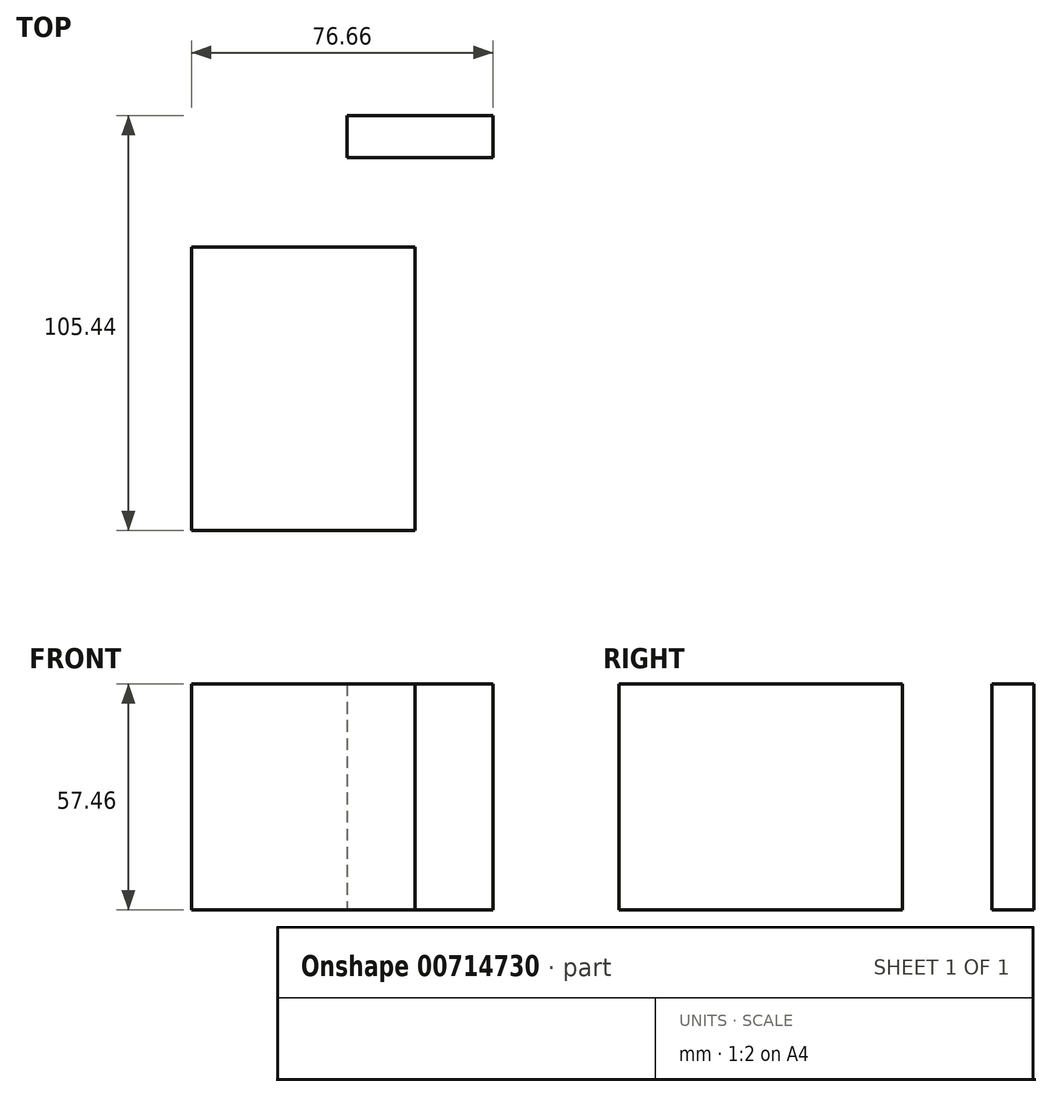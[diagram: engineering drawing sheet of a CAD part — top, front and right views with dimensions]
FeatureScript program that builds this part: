
annotation { "Feature Type Name" : "Feature", "Feature Type Description" : "" }
export const myFeature = defineFeature(function(context is Context, id is Id, definition is map)
    precondition{}
    {
        {
            var Q0;
            Q0=qCreatedBy(makeId("Top.planeOp"),FACE);
            var sketch = newSketch(context, id + "F0", { "sketchPlane" : qUnion([Q0])});
            skLineSegment(sketch, "E0.bottom", {"start": v(56.86, 0) * mm, "end": v(0, 0) * mm});
            skLineSegment(sketch, "E0.top", {"start": v(56.86, 72.05) * mm, "end": v(0, 72.05) * mm});
            skLineSegment(sketch, "E0.left", {"start": v(56.86, 0) * mm, "end": v(56.86, 72.05) * mm});
            skLineSegment(sketch, "E0.right", {"start": v(0, 0) * mm, "end": v(0, 72.05) * mm});
            skLineSegment(sketch, "E1.bottom", {"start": v(76.66, 94.67) * mm, "end": v(39.56, 94.67) * mm});
            skLineSegment(sketch, "E1.top", {"start": v(76.66, 105.44) * mm, "end": v(39.56, 105.44) * mm});
            skLineSegment(sketch, "E1.left", {"start": v(76.66, 94.67) * mm, "end": v(76.66, 105.44) * mm});
            skLineSegment(sketch, "E1.right", {"start": v(39.56, 94.67) * mm, "end": v(39.56, 105.44) * mm});
            skSolve(sketch);
        }
        {
            var Q0;
            Q0 = qSketchRegion(id + "F0", true);
            extrude(context, id + "F1", {"entities" : qUnion([Q0]), "depth" : 57.46 * mm, "offsetDistance" : 25.4 * mm});
        }
    });
